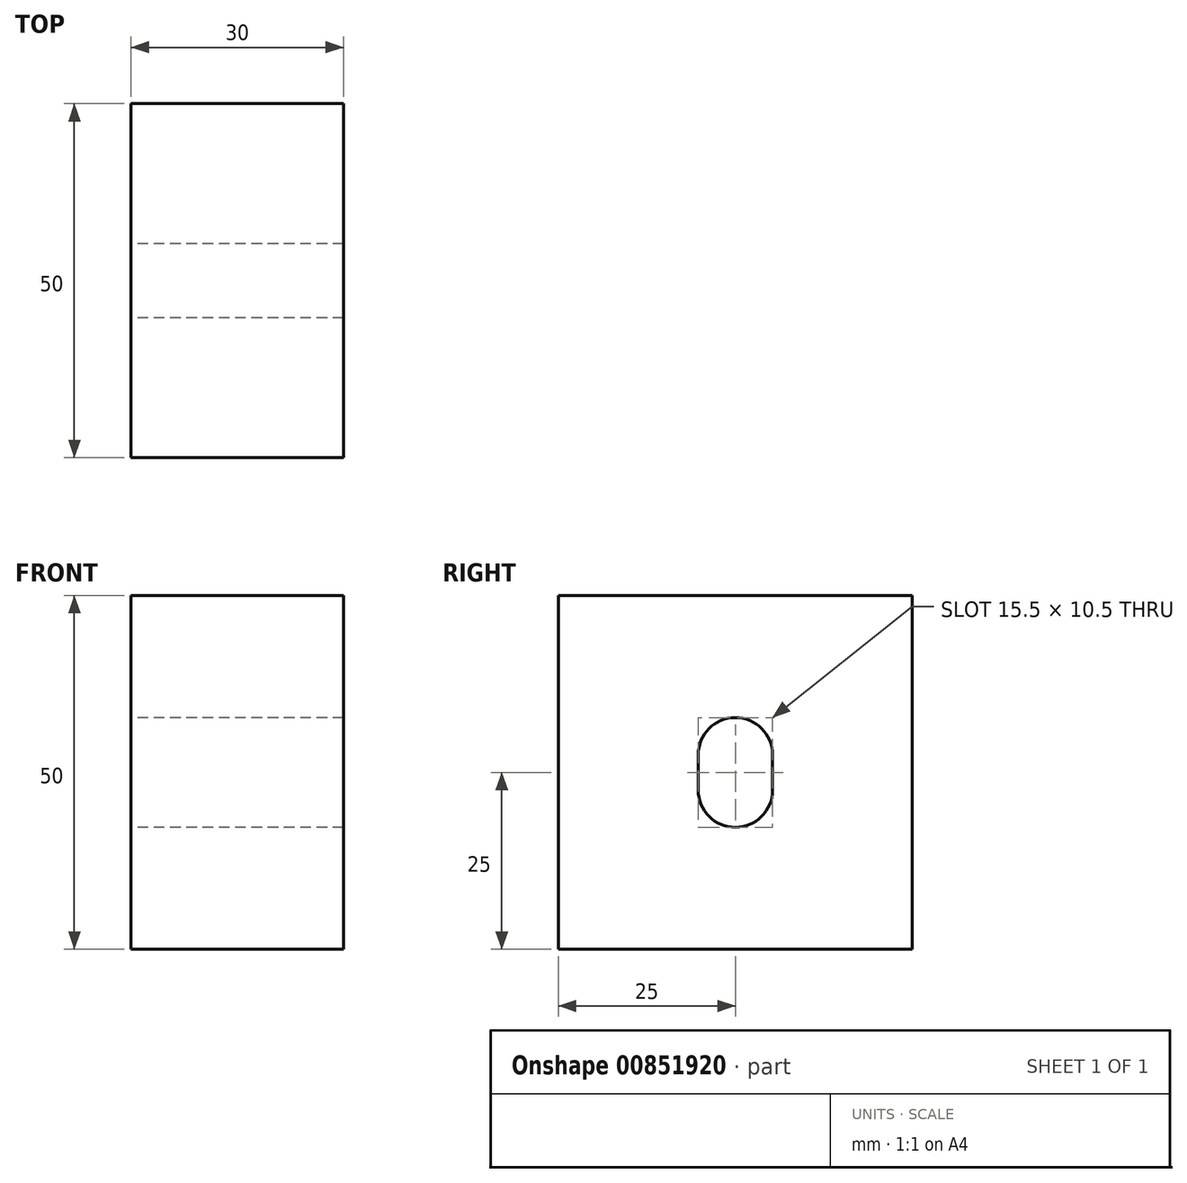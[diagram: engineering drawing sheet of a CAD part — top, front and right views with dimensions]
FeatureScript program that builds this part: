
annotation { "Feature Type Name" : "Feature", "Feature Type Description" : "" }
export const myFeature = defineFeature(function(context is Context, id is Id, definition is map)
    precondition{}
    {
        {
            var Q0;
            Q0=qCreatedBy(makeId("Right.planeOp"),FACE);
            var sketch = newSketch(context, id + "F0", { "sketchPlane" : qUnion([Q0])});
            skLineSegment(sketch, "E0.bottom", {"start": v(25, -25) * mm, "end": v(-25, -25) * mm});
            skLineSegment(sketch, "E0.top", {"start": v(25, 25) * mm, "end": v(-25, 25) * mm});
            skLineSegment(sketch, "E0.left", {"start": v(25, -25) * mm, "end": v(25, 25) * mm});
            skLineSegment(sketch, "E0.right", {"start": v(-25, -25) * mm, "end": v(-25, 25) * mm});
            skPoint(sketch, "E0.middle", {"position": v(0, 0) * mm});
            skLineSegment(sketch, "E1", {"start": v(0, 2.5) * mm, "end": v(0, -2.5) * mm});
            skArc(sketch, "E2.0.startCap", {"start": v(-5.25, 2.5) * mm, "mid": v(0, 7.75) * mm, "end": v(5.25, 2.5) * mm});
            skArc(sketch, "E2.0.endCap", {"start": v(5.25, -2.5) * mm, "mid": v(0, -7.75) * mm, "end": v(-5.25, -2.5) * mm});
            skLineSegment(sketch, "E2.0.left", {"start": v(5.25, 2.5) * mm, "end": v(5.25, -2.5) * mm});
            skLineSegment(sketch, "E2.0.right", {"start": v(-5.25, 2.5) * mm, "end": v(-5.25, -2.5) * mm});
            skSolve(sketch);
        }
        {
            var Q0;
            Q0=makeQuery(id+"F0.imprint","IMPRINT",FACE,{"disambiguationData":[TD([[makeQuery(id+"F0.imprint","IMPRINT",EDGE,{"derivedFrom":sQuery(id+"F0.wireOp",EDGE,"E0.bottom")}),-1.0]])]});
            extrude(context, id + "F1", {"entities" : qUnion([Q0]), "depth" : 30 * mm, "offsetDistance" : 25 * mm, "symmetric" : true});
        }
    });
